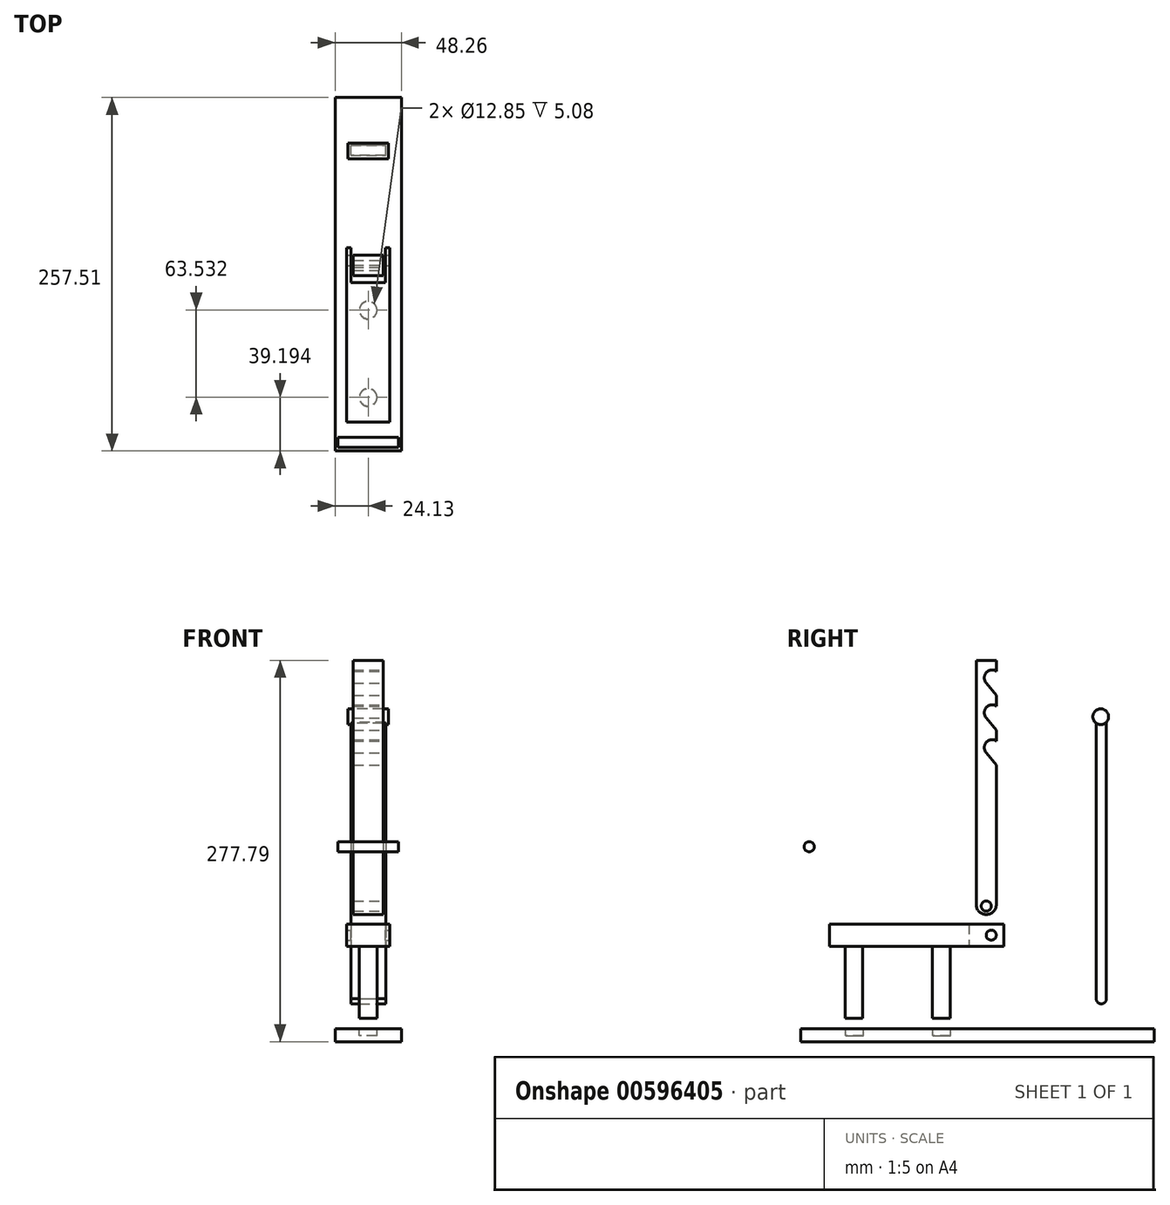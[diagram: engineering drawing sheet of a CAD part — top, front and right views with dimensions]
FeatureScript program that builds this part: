
annotation { "Feature Type Name" : "Feature", "Feature Type Description" : "" }
export const myFeature = defineFeature(function(context is Context, id is Id, definition is map)
    precondition{}
    {
        {
            var Q0;
            Q0=qCreatedBy(makeId("Front.planeOp"),FACE);
            var sketch = newSketch(context, id + "F0", { "sketchPlane" : qUnion([Q0])});
            skLineSegment(sketch, "E0.bottom", {"start": v(-10.87, 88.9) * mm, "end": v(10.87, 88.9) * mm});
            skLineSegment(sketch, "E0.top", {"start": v(-10.87, -88.9) * mm, "end": v(10.87, -88.9) * mm});
            skLineSegment(sketch, "E0.left", {"start": v(-10.87, 88.9) * mm, "end": v(-10.87, -88.9) * mm});
            skLineSegment(sketch, "E0.right", {"start": v(10.87, 88.9) * mm, "end": v(10.87, -88.9) * mm});
            skPoint(sketch, "E0.middle", {"position": v(0, 0) * mm});
            skSolve(sketch);
        }
        {
            var Q0;
            Q0 = qSketchRegion(id + "F0", true);
            extrude(context, id + "F1", {"entities" : qUnion([Q0]), "depth" : 14.73 * mm, "offsetDistance" : 25.4 * mm});
        }
        {
            var Q0;
            Q0=qCreatedBy(makeId("Right.planeOp"),FACE);
            var sketch = newSketch(context, id + "F2", { "sketchPlane" : qUnion([Q0])});
            skLineSegment(sketch, "E1", {"start": v(0, 0) * mm, "end": v(0, 25.4) * mm});
            skLineSegment(sketch, "E2", {"start": v(0, 25.4) * mm, "end": v(0, 50.8) * mm});
            skLineSegment(sketch, "E3", {"start": v(0, 50.8) * mm, "end": v(0, 76.2) * mm});
            skLineSegment(sketch, "E4", {"start": v(0, 25.4) * mm, "end": v(-3.1, 25.4) * mm});
            skLineSegment(sketch, "E5", {"start": v(0, 50.8) * mm, "end": v(-3.1, 50.8) * mm});
            skCircle(sketch, "E6", {"center": v(-3.1, 76.2) * mm, "radius": 5.72 * mm});
            skCircle(sketch, "E7", {"center": v(-3.1, 50.8) * mm, "radius": 5.72 * mm});
            skCircle(sketch, "E8", {"center": v(-3.1, 25.4) * mm, "radius": 5.72 * mm});
            skLineSegment(sketch, "E9", {"start": v(-3.1, 50.8) * mm, "end": v(-8.81, 50.8) * mm});
            skLineSegment(sketch, "E10", {"start": v(-3.1, 25.4) * mm, "end": v(-8.82, 25.4) * mm});
            skLineSegment(sketch, "E11", {"start": v(-7.14, 46.76) * mm, "end": v(0, 38.1) * mm});
            skLineSegment(sketch, "E12", {"start": v(0, 38.1) * mm, "end": v(0, 50.8) * mm});
            skLineSegment(sketch, "E13", {"start": v(-7.14, 72.16) * mm, "end": v(0, 63.5) * mm});
            skLineSegment(sketch, "E14", {"start": v(0, 63.5) * mm, "end": v(-7.14, 72.16) * mm});
            skLineSegment(sketch, "E15", {"start": v(-7.15, 21.36) * mm, "end": v(0, 12.69) * mm});
            skLineSegment(sketch, "E16", {"start": v(0, 12.69) * mm, "end": v(0, 25.4) * mm});
            skLineSegment(sketch, "E17", {"start": v(0, 63.5) * mm, "end": v(2.62, 76.09) * mm});
            skLineSegment(sketch, "E18", {"start": v(0, 38.1) * mm, "end": v(2.62, 50.77) * mm});
            skLineSegment(sketch, "E19", {"start": v(0, 12.69) * mm, "end": v(2.6, 25.42) * mm});
            skSolve(sketch);
        }
        {
            var Q0;
            Q0 = qSketchRegion(id + "F2", true);
            extrude(context, id + "F3", {"entities" : qUnion([Q0]), "operationType" : NewBodyOperationType.REMOVE, "endBound" : BoundingType.SYMMETRIC, "oppositeDirection" : true, "depth" : 25.4 * mm, "offsetDistance" : 25.4 * mm});
        }
        {
            var Q0;
            Q0=qCreatedBy(makeId("Right.planeOp"),FACE);
            var sketch = newSketch(context, id + "F4", { "sketchPlane" : qUnion([Q0])});
            skCircle(sketch, "E20", {"center": v(76.03, 47.8) * mm, "radius": 5.72 * mm});
            skLineSegment(sketch, "E21.top", {"start": v(80.15, 152.75) * mm, "end": v(72.77, 152.75) * mm});
            skLineSegment(sketch, "E21.left", {"start": v(80.15, -68.54) * mm, "end": v(80.15, 43.85) * mm});
            skLineSegment(sketch, "E21.right", {"start": v(72.77, -68.54) * mm, "end": v(72.77, 43.11) * mm});
            skPoint(sketch, "E21.middle", {"position": v(76.46, 42.1) * mm});
            skLineSegment(sketch, "E22", {"start": v(1.55, 0) * mm, "end": v(-1.55, 0) * mm});
            skLineSegment(sketch, "E23", {"start": v(72.77, -68.54) * mm, "end": v(72.77, -157.66) * mm});
            skLineSegment(sketch, "E24", {"start": v(72.77, -157.66) * mm, "end": v(72.77, -157.65) * mm});
            skLineSegment(sketch, "E25", {"start": v(72.74, -157.65) * mm, "end": v(80.15, -157.65) * mm});
            skLineSegment(sketch, "E26", {"start": v(80.15, -68.54) * mm, "end": v(80.15, -157.65) * mm});
            skPoint(sketch, "E27.orphan", {"position": v(98.93, -157.66) * mm});
            skSolve(sketch);
        }
        {
            var Q0;
            {var subQ0=sQuery(id+"F4.wireOp",EDGE,"E20");var subQ1=makeQuery(id+"F4.imprint","INTERSECT",VERTEX,{"derivedFrom":[subQ0,sQuery(id+"F4.wireOp",EDGE,"E21.left")]});Q0=makeQuery(id+"F4.imprint","IMPRINT",FACE,{"disambiguationData":[TD([[makeQuery(id+"F4.imprint","IMPRINT",EDGE,{"disambiguationData":[TD([[subQ1,1.0]])],"derivedFrom":subQ0}),1.0]])]});}
            extrude(context, id + "F5", {"entities" : qUnion([Q0]), "endBound" : BoundingType.SYMMETRIC, "depth" : 29.46 * mm, "offsetDistance" : 25.4 * mm});
        }
        {
            var Q0;
            Q0=makeQuery(id+"F1.opExtrude","SWEPT_FACE",FACE,{"disambiguationData":[OSD([sQuery(id+"F0.wireOp",EDGE,"E0.right")])]});
            var sketch = newSketch(context, id + "F6", { "sketchPlane" : qUnion([Q0])});
            skCircle(sketch, "E28", {"center": v(-7.37, -88.9) * mm, "radius": 7.37 * mm});
            skSolve(sketch);
        }
        {
            var Q0;
            {var subQ1=sQuery(id+"F0.wireOp",EDGE,"E0.right");var subQ2=sQuery(id+"F0.wireOp",EDGE,"E0.top");var subQ3=makeQuery(id+"F1.opExtrude","SWEPT_EDGE",EDGE,{"disambiguationData":[OSD([subQ2,subQ1])]});Q0=makeQuery(id+"F6.imprint","IMPRINT",FACE,{"disambiguationData":[TD([[makeQuery(id+"F6.imprint","IMPRINT",EDGE,{"derivedFrom":subQ3}),-1.0]])]});}
            var Q1;
            Q1=sQuery(id+"F6.wireOp",EDGE,"E28");
            var Q2;
            Q2=makeQuery(id+"F1.opExtrude","SWEPT_FACE",FACE,{"disambiguationData":[OSD([sQuery(id+"F0.wireOp",EDGE,"E0.left")])]});
            extrude(context, id + "F7", {"entities" : qUnion([Q0]), "operationType" : NewBodyOperationType.ADD, "surfaceEntities" : qUnion([Q1]), "endBound" : BoundingType.UP_TO_SURFACE, "oppositeDirection" : true, "depth" : 25.4 * mm, "endBoundEntityFace" : qUnion([Q2]), "offsetDistance" : 25.4 * mm});
        }
        {
            var Q0;
            Q0=qCreatedBy(makeId("Right.planeOp"),FACE);
            var sketch = newSketch(context, id + "F8", { "sketchPlane" : qUnion([Q0])});
            skLineSegment(sketch, "E29.bottom", {"start": v(5.52, -103.16) * mm, "end": v(-121.48, -103.16) * mm});
            skLineSegment(sketch, "E29.top", {"start": v(5.52, -119.4) * mm, "end": v(-121.48, -119.4) * mm});
            skLineSegment(sketch, "E29.left", {"start": v(5.52, -103.16) * mm, "end": v(5.52, -119.4) * mm});
            skLineSegment(sketch, "E29.right", {"start": v(-121.48, -103.16) * mm, "end": v(-121.48, -119.4) * mm});
            skPoint(sketch, "E29.middle", {"position": v(-57.98, -111.28) * mm});
            skSolve(sketch);
        }
        {
            var Q0;
            Q0 = qSketchRegion(id + "F8", true);
            extrude(context, id + "F9", {"entities" : qUnion([Q0]), "endBound" : BoundingType.SYMMETRIC, "depth" : 31.5 * mm, "offsetDistance" : 25.4 * mm});
        }
        {
            var Q0;
            Q0=makeQuery(id+"F9.opExtrude","SWEPT_FACE",FACE,{"disambiguationData":[OSD([sQuery(id+"F8.wireOp",EDGE,"E29.left")])]});
            var sketch = newSketch(context, id + "F10", { "sketchPlane" : qUnion([Q0])});
            skLineSegment(sketch, "E30.bottom", {"start": v(-12.45, -99.54) * mm, "end": v(12.45, -99.54) * mm});
            skLineSegment(sketch, "E30.top", {"start": v(-12.45, -123.23) * mm, "end": v(12.45, -123.23) * mm});
            skLineSegment(sketch, "E30.left", {"start": v(-12.45, -99.54) * mm, "end": v(-12.45, -123.23) * mm});
            skLineSegment(sketch, "E30.right", {"start": v(12.45, -99.54) * mm, "end": v(12.45, -123.23) * mm});
            skPoint(sketch, "E30.middle", {"position": v(0, -111.38) * mm});
            skSolve(sketch);
        }
        {
            var Q0;
            Q0 = qSketchRegion(id + "F10", true);
            extrude(context, id + "F11", {"entities" : qUnion([Q0]), "operationType" : NewBodyOperationType.REMOVE, "oppositeDirection" : true, "depth" : 25.4 * mm, "offsetDistance" : 25.4 * mm});
        }
        {
            var Q0;
            {var subQ0=sQuery(id+"F0.wireOp",EDGE,"E0.right");Q0=makeQuery(id+"F7.boolean.opBoolean","MERGE",FACE,{"derivedFrom":[makeQuery(id+"F1.opExtrude","SWEPT_FACE",FACE,{"disambiguationData":[OSD([subQ0])]}),makeQuery(id+"F7.opExtrude","CAP_FACE",FACE,{"disambiguationData":[OSD([sQuery(id+"F0.wireOp",EDGE,"E0.top"),subQ0,sQuery(id+"F6.wireOp",EDGE,"E28")])],"isStart":true})]});}
            var sketch = newSketch(context, id + "F12", { "sketchPlane" : qUnion([Q0])});
            skCircle(sketch, "E31", {"center": v(-7.37, -90.13) * mm, "radius": 3.68 * mm});
            skPoint(sketch, "E31.centerSnap0", {"position": v(-7.37, -96.27) * mm});
            skSolve(sketch);
        }
        {
            var Q0;
            Q0 = qSketchRegion(id + "F12", true);
            extrude(context, id + "F13", {"entities" : qUnion([Q0]), "operationType" : NewBodyOperationType.REMOVE, "oppositeDirection" : true, "depth" : 25.4 * mm, "offsetDistance" : 25.4 * mm});
        }
        {
            var Q0;
            Q0=makeQuery(id+"F9.opExtrude","CAP_FACE",FACE,{"disambiguationData":[OSD([sQuery(id+"F8.wireOp",EDGE,"E29.bottom"),sQuery(id+"F8.wireOp",EDGE,"E29.top"),sQuery(id+"F8.wireOp",EDGE,"E29.left"),sQuery(id+"F8.wireOp",EDGE,"E29.right")])],"isStart":false});
            var sketch = newSketch(context, id + "F14", { "sketchPlane" : qUnion([Q0])});
            skCircle(sketch, "E32", {"center": v(-3.76, -111.28) * mm, "radius": 3.68 * mm});
            skPoint(sketch, "E32.centerSnap0", {"position": v(5.52, -111.28) * mm});
            skSolve(sketch);
        }
        {
            var Q0;
            Q0 = qSketchRegion(id + "F14", true);
            extrude(context, id + "F15", {"entities" : qUnion([Q0]), "operationType" : NewBodyOperationType.REMOVE, "oppositeDirection" : true, "depth" : 35.66 * mm, "offsetDistance" : 25.4 * mm});
        }
        {
            var Q0;
            Q0=qCreatedBy(makeId("Right.planeOp"),FACE);
            var sketch = newSketch(context, id + "F16", { "sketchPlane" : qUnion([Q0])});
            skCircle(sketch, "E33", {"center": v(-136.36, -46.87) * mm, "radius": 3.68 * mm});
            skSolve(sketch);
        }
        {
            var Q0;
            Q0 = qSketchRegion(id + "F16", true);
            extrude(context, id + "F17", {"entities" : qUnion([Q0]), "endBound" : BoundingType.SYMMETRIC, "depth" : 44.2 * mm, "offsetDistance" : 25.4 * mm});
        }
        {
            var Q0;
            {var subQ4=sQuery(id+"F4.wireOp",EDGE,"E21.left");Q0=makeQuery(id+"F4.imprint","IMPRINT",FACE,{"disambiguationData":[TD([[makeQuery(id+"F4.imprint","IMPRINT",EDGE,{"derivedFrom":subQ4}),1.0]])]});}
            extrude(context, id + "F18", {"entities" : qUnion([Q0]), "operationType" : NewBodyOperationType.ADD, "endBound" : BoundingType.SYMMETRIC, "depth" : 25.4 * mm, "offsetDistance" : 25.4 * mm});
        }
        {
            var Q0;
            Q0=qCreatedBy(makeId("Right.planeOp"),FACE);
            var sketch = newSketch(context, id + "F19", { "sketchPlane" : qUnion([Q0])});
            skLineSegment(sketch, "E34.bottom", {"start": v(-142.6, -179.33) * mm, "end": v(114.9, -179.33) * mm});
            skLineSegment(sketch, "E34.top", {"start": v(-142.6, -188.9) * mm, "end": v(114.9, -188.9) * mm});
            skLineSegment(sketch, "E34.left", {"start": v(-142.6, -179.33) * mm, "end": v(-142.6, -188.9) * mm});
            skLineSegment(sketch, "E34.right", {"start": v(114.9, -179.33) * mm, "end": v(114.9, -188.9) * mm});
            skPoint(sketch, "E34.middle", {"position": v(-13.85, -184.1) * mm});
            skSolve(sketch);
        }
        {
            var Q0;
            Q0 = qSketchRegion(id + "F19", true);
            extrude(context, id + "F20", {"entities" : qUnion([Q0]), "endBound" : BoundingType.SYMMETRIC, "depth" : 48.26 * mm, "offsetDistance" : 25.4 * mm});
        }
        {
            var Q0;
            Q0=makeQuery(id+"F9.opExtrude","SWEPT_FACE",FACE,{"disambiguationData":[OSD([sQuery(id+"F8.wireOp",EDGE,"E29.top")])]});
            var sketch = newSketch(context, id + "F21", { "sketchPlane" : qUnion([Q0])});
            skCircle(sketch, "E35", {"center": v(0, 103.73) * mm, "radius": 6.42 * mm});
            skPoint(sketch, "E35.centerSnap0", {"position": v(0, 121.48) * mm});
            skCircle(sketch, "E36", {"center": v(0, 40.2) * mm, "radius": 6.43 * mm});
            skPoint(sketch, "E36.centerSnap0", {"position": v(0, 19.88) * mm});
            skSolve(sketch);
        }
        {
            var Q0;
            Q0 = qSketchRegion(id + "F21", true);
            extrude(context, id + "F22", {"entities" : qUnion([Q0]), "operationType" : NewBodyOperationType.ADD, "depth" : 52.58 * mm, "offsetDistance" : 25.4 * mm});
        }
        {
            var Q0;
            Q0=makeQuery(id+"F20.opExtrude","SWEPT_FACE",FACE,{"disambiguationData":[OSD([sQuery(id+"F19.wireOp",EDGE,"E34.bottom")])]});
            var sketch = newSketch(context, id + "F23", { "sketchPlane" : qUnion([Q0])});
            skCircle(sketch, "E37", {"center": v(0, -103.4) * mm, "radius": 6.43 * mm});
            skPoint(sketch, "E37.centerSnap0", {"position": v(0, -142.6) * mm});
            skLineSegment(sketch, "E38", {"start": v(0, -103.4) * mm, "end": v(0, -39.87) * mm});
            skCircle(sketch, "E39", {"center": v(0, -39.87) * mm, "radius": 6.43 * mm});
            skSolve(sketch);
        }
        {
            var Q0;
            Q0 = qSketchRegion(id + "F23", true);
            extrude(context, id + "F24", {"entities" : qUnion([Q0]), "operationType" : NewBodyOperationType.REMOVE, "oppositeDirection" : true, "depth" : 5.08 * mm, "offsetDistance" : 25.4 * mm});
        }
        {
            var Q0;
            Q0=makeQuery(id+"F18.opExtrude","CAP_FACE",FACE,{"disambiguationData":[OSD([sQuery(id+"F4.wireOp",EDGE,"E20"),sQuery(id+"F4.wireOp",EDGE,"E21.left"),sQuery(id+"F4.wireOp",EDGE,"E21.right"),sQuery(id+"F4.wireOp",EDGE,"E23"),sQuery(id+"F4.wireOp",EDGE,"E25"),sQuery(id+"F4.wireOp",EDGE,"E26")])],"isStart":false});
            var sketch = newSketch(context, id + "F25", { "sketchPlane" : qUnion([Q0])});
            skCircle(sketch, "E40", {"center": v(76.46, -157.65) * mm, "radius": 3.7 * mm});
            skSolve(sketch);
        }
        {
            var Q0;
            Q0 = qSketchRegion(id + "F25", true);
            extrude(context, id + "F26", {"entities" : qUnion([Q0]), "operationType" : NewBodyOperationType.ADD, "oppositeDirection" : true, "depth" : 25.4 * mm, "offsetDistance" : 25.4 * mm});
        }
    });
